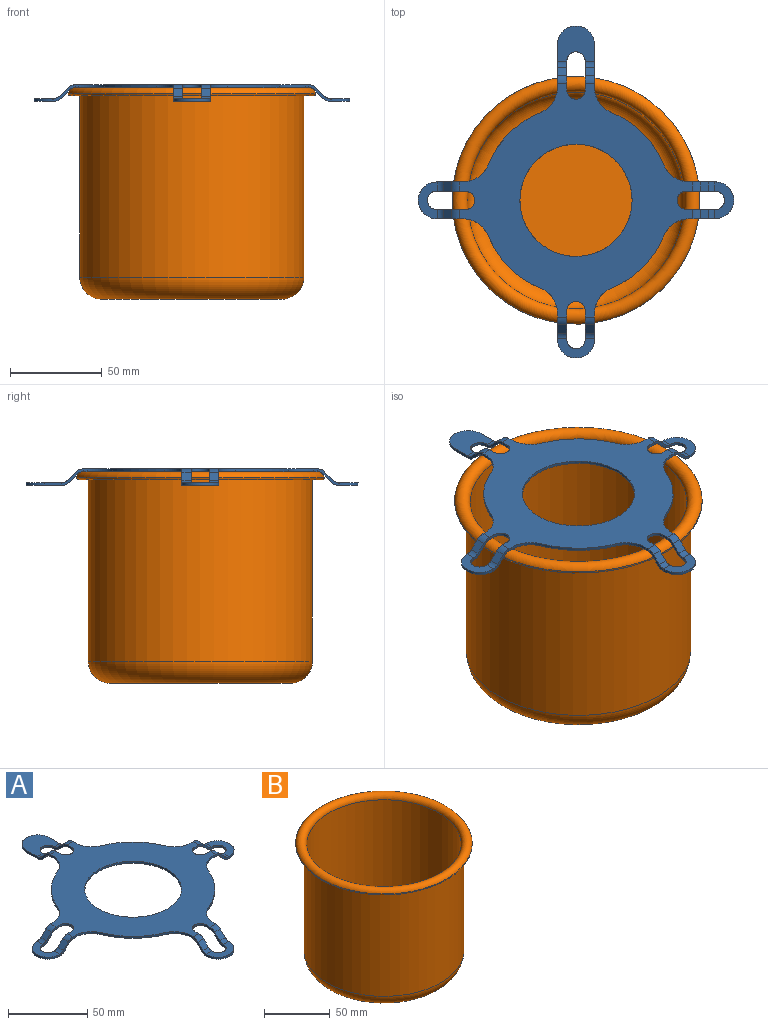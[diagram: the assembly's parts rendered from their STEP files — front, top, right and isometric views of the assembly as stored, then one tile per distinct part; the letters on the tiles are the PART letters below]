
ASSEMBLY  parts=2 mates=1
PART A: 163 faces, bbox 172.9x181.9x10 mm
  f0: plane 20x10.56mm, normal (0,0,-1), area 121.5mm2, adj f8,f9,f10,f11,f12,f13,f22,f23
  f1: plane 20x10.56mm, normal (0,0,-1), area 121.5mm2, adj f14,f15,f16,f17,f18,f19,f24,f25
  f2: plane 20x10.57mm, normal (0,0,-1), area 121.7mm2, adj f3,f4,f5,f6,f7,f20,f21,f26
  f3: cylinder r=10mm len=20mm, axis (0,0,1), area 47.1mm2, adj f2,f7,f20,f28
  f4: cylinder r=5mm len=10mm, axis (0,0,-1), area 23.6mm2, adj f2,f5,f6,f28
  f5: plane 1.5x0.39mm, normal (0,1,0), area 0.6mm2, adj f2,f4,f27,f28
  f6: plane 1.5x0.39mm, normal (0,-1,0), area 0.6mm2, adj f2,f4,f28,f29
  f7: plane 1.5x0.39mm, normal (0,1,0), area 0.6mm2, adj f2,f3,f28,f30
  f8: plane 1.5x0.38mm, normal (0,1,0), area 0.6mm2, adj f0,f9,f31,f33
  f9: cylinder r=10mm len=20mm, axis (0,0,1), area 47.1mm2, adj f0,f8,f13,f33
  f10: cylinder r=5mm len=10mm, axis (0,0,-1), area 23.6mm2, adj f0,f11,f12,f33
  f11: plane 1.5x0.39mm, normal (0,-1,0), area 0.6mm2, adj f0,f10,f32,f33
  f12: plane 1.5x0.39mm, normal (0,1,0), area 0.6mm2, adj f0,f10,f33,f34
  f13: plane 1.5x0.38mm, normal (0,-1,0), area 0.6mm2, adj f0,f9,f33,f35
  f14: plane 1.5x0.38mm, normal (-1,0,0), area 0.6mm2, adj f1,f15,f36,f38
  f15: cylinder r=10mm len=20mm, axis (0,0,1), area 47.1mm2, adj f1,f14,f19,f38
  f16: cylinder r=5mm len=10mm, axis (0,0,-1), area 23.6mm2, adj f1,f17,f18,f38
  f17: plane 1.5x0.39mm, normal (1,0,0), area 0.6mm2, adj f1,f16,f37,f38
  f18: plane 1.5x0.39mm, normal (-1,0,0), area 0.6mm2, adj f1,f16,f38,f39
  f19: plane 1.5x0.38mm, normal (1,0,0), area 0.6mm2, adj f1,f15,f38,f40
  f20: plane 1.5x0.39mm, normal (0,-1,0), area 0.6mm2, adj f2,f3,f28,f41
  f21: cylinder r=6mm len=5mm, axis (0,-1,0), area 23.6mm2, adj f2,f29,f30,f42
  f22: cylinder r=6mm len=5mm, axis (0,1,0), area 23.6mm2, adj f0,f31,f32,f43
  f23: cylinder r=6mm len=5mm, axis (0,1,0), area 23.6mm2, adj f0,f34,f35,f44
  f24: cylinder r=6mm len=5mm, axis (-1,0,0), area 23.6mm2, adj f1,f36,f37,f45
  f25: cylinder r=6mm len=5mm, axis (-1,0,0), area 23.6mm2, adj f1,f39,f40,f46
  f26: cylinder r=6mm len=5mm, axis (0,-1,0), area 23.6mm2, adj f2,f27,f41,f47
  f27: plane 4.24x2.82mm, normal (0,1,0), area 6.2mm2, adj f5,f26,f48,f49
  f28: plane 20.31x10.7mm, normal (0,0,1), area 122mm2, adj f3,f4,f5,f6,f7,f20,f48,f50
  f29: plane 4.24x2.82mm, normal (0,-1,0), area 6.2mm2, adj f6,f21,f50,f51
  f30: plane 4.24x2.82mm, normal (0,1,0), area 6.2mm2, adj f7,f21,f50,f52
  f31: plane 4.24x2.82mm, normal (0,1,0), area 6.2mm2, adj f8,f22,f53,f54
  f32: plane 4.24x2.82mm, normal (0,-1,0), area 6.2mm2, adj f11,f22,f53,f55
  f33: plane 20.31x10.69mm, normal (0,0,1), area 121.6mm2, adj f8,f9,f10,f11,f12,f13,f53,f56
  f34: plane 4.24x2.82mm, normal (0,1,0), area 6.2mm2, adj f12,f23,f56,f57
  f35: plane 4.24x2.82mm, normal (0,-1,0), area 6.2mm2, adj f13,f23,f56,f58
  f36: plane 4.24x2.82mm, normal (-1,0,0), area 6.2mm2, adj f14,f24,f59,f60
  f37: plane 4.24x2.82mm, normal (1,0,0), area 6.2mm2, adj f17,f24,f59,f61
  f38: plane 20.31x10.69mm, normal (0,0,1), area 121.5mm2, adj f14,f15,f16,f17,f18,f19,f59,f62
  f39: plane 4.24x2.82mm, normal (-1,0,0), area 6.2mm2, adj f18,f25,f62,f63
  f40: plane 4.24x2.82mm, normal (1,0,0), area 6.2mm2, adj f19,f25,f62,f64
  f41: plane 4.24x2.82mm, normal (0,-1,0), area 6.2mm2, adj f20,f26,f48,f65
  f42: plane 5x4.44mm, normal (-0.71,0,-0.71), area 31.4mm2, adj f21,f51,f52,f66
  f43: plane 5x4.44mm, normal (0.71,0,-0.71), area 31.4mm2, adj f22,f54,f55,f67
  f44: plane 5x4.44mm, normal (0.71,0,-0.71), area 31.4mm2, adj f23,f57,f58,f68
  f45: plane 5x4.44mm, normal (0,0.71,-0.71), area 31.4mm2, adj f24,f60,f61,f69
  f46: plane 5x4.44mm, normal (0,0.71,-0.71), area 31.4mm2, adj f25,f63,f64,f70
  f47: plane 5x4.44mm, normal (-0.71,0,-0.71), area 31.4mm2, adj f26,f49,f65,f71
  f48: cylinder r=4.5mm len=5mm, axis (0,-1,0), area 17.7mm2, adj f27,f28,f41,f72
  f49: plane 5.5x5.5mm, normal (0,1,0), area 9.4mm2, adj f27,f47,f72,f73
  f50: cylinder r=4.5mm len=5mm, axis (0,-1,0), area 17.7mm2, adj f28,f29,f30,f75
  f51: plane 5.5x5.5mm, normal (0,-1,0), area 9.4mm2, adj f29,f42,f74,f75
  f52: plane 5.5x5.5mm, normal (0,1,0), area 9.4mm2, adj f30,f42,f75,f76
  f53: cylinder r=4.5mm len=5mm, axis (0,1,0), area 17.7mm2, adj f31,f32,f33,f78
  f54: plane 5.5x5.5mm, normal (0,1,0), area 9.4mm2, adj f31,f43,f77,f78
  f55: plane 5.5x5.5mm, normal (0,-1,0), area 9.4mm2, adj f32,f43,f78,f79
  f56: cylinder r=4.5mm len=5mm, axis (0,1,0), area 17.7mm2, adj f33,f34,f35,f81
  f57: plane 5.5x5.5mm, normal (0,1,0), area 9.4mm2, adj f34,f44,f80,f81
  f58: plane 5.5x5.5mm, normal (0,-1,0), area 9.4mm2, adj f35,f44,f81,f82
  f59: cylinder r=4.5mm len=5mm, axis (-1,0,0), area 17.7mm2, adj f36,f37,f38,f84
  f60: plane 5.5x5.5mm, normal (-1,0,0), area 9.4mm2, adj f36,f45,f83,f84
  f61: plane 5.5x5.5mm, normal (1,0,0), area 9.4mm2, adj f37,f45,f84,f85
  f62: cylinder r=4.5mm len=5mm, axis (-1,0,0), area 17.7mm2, adj f38,f39,f40,f87
  f63: plane 5.5x5.5mm, normal (-1,0,0), area 9.4mm2, adj f39,f46,f86,f87
  f64: plane 5.5x5.5mm, normal (1,0,0), area 9.4mm2, adj f40,f46,f87,f88
  f65: plane 5.5x5.5mm, normal (0,-1,0), area 9.4mm2, adj f41,f47,f72,f89
  f66: cylinder r=4.5mm len=5mm, axis (0,-1,0), area 17.7mm2, adj f42,f74,f76,f90
  f67: cylinder r=4.5mm len=5mm, axis (0,1,0), area 17.7mm2, adj f43,f77,f79,f90
  f68: cylinder r=4.5mm len=5mm, axis (0,1,0), area 17.7mm2, adj f44,f80,f82,f90
  f69: cylinder r=4.5mm len=5mm, axis (-1,0,0), area 17.7mm2, adj f45,f83,f85,f90
  f70: cylinder r=4.5mm len=5mm, axis (-1,0,0), area 17.7mm2, adj f46,f86,f88,f90
  f71: cylinder r=4.5mm len=5mm, axis (0,-1,0), area 17.7mm2, adj f47,f73,f89,f90
  f72: plane 5x4.44mm, normal (0.71,0,0.71), area 31.4mm2, adj f48,f49,f65,f91
  f73: plane 4.24x2.82mm, normal (0,1,0), area 6.2mm2, adj f49,f71,f91,f92
  f74: plane 4.24x2.82mm, normal (0,-1,0), area 6.2mm2, adj f51,f66,f94,f95
  f75: plane 5x4.44mm, normal (0.71,0,0.71), area 31.4mm2, adj f50,f51,f52,f95
  f76: plane 4.24x2.82mm, normal (0,1,0), area 6.2mm2, adj f52,f66,f95,f96
  f77: plane 4.24x2.82mm, normal (0,1,0), area 6.2mm2, adj f54,f67,f105,f106
  f78: plane 5x4.44mm, normal (-0.71,0,0.71), area 31.4mm2, adj f53,f54,f55,f106
  f79: plane 4.24x2.82mm, normal (0,-1,0), area 6.2mm2, adj f55,f67,f106,f107
  f80: plane 4.24x2.82mm, normal (0,1,0), area 6.2mm2, adj f57,f68,f109,f110
  f81: plane 5x4.44mm, normal (-0.71,0,0.71), area 31.4mm2, adj f56,f57,f58,f110
  f82: plane 4.24x2.82mm, normal (0,-1,0), area 6.2mm2, adj f58,f68,f110,f111
  f83: plane 4.24x2.82mm, normal (-1,0,0), area 6.2mm2, adj f60,f69,f115,f116
  f84: plane 5x4.44mm, normal (0,-0.71,0.71), area 31.4mm2, adj f59,f60,f61,f116
  f85: plane 4.24x2.82mm, normal (1,0,0), area 6.2mm2, adj f61,f69,f116,f117
  f86: plane 4.24x2.82mm, normal (-1,0,0), area 6.2mm2, adj f63,f70,f119,f120
  f87: plane 5x4.44mm, normal (0,-0.71,0.71), area 31.4mm2, adj f62,f63,f64,f120
  f88: plane 4.24x2.82mm, normal (1,0,0), area 6.2mm2, adj f64,f70,f120,f121
  f89: plane 4.24x2.82mm, normal (0,-1,0), area 6.2mm2, adj f65,f71,f91,f125
  f90: plane 127.02x127.02mm, normal (0,0,-1), area 6269.3mm2, adj f66,f67,f68,f69,f70,f71,f92,f93
  f91: cylinder r=6mm len=5mm, axis (0,-1,0), area 23.6mm2, adj f72,f73,f89,f133
  f92: plane 3.52x1.5mm, normal (0,1,0), area 5.3mm2, adj f73,f90,f93,f133
  f93: cylinder r=5mm len=10mm, axis (0,0,-1), area 23.6mm2, adj f90,f92,f94,f133
  f94: plane 3.52x1.5mm, normal (0,-1,0), area 5.3mm2, adj f74,f90,f93,f133
  f95: cylinder r=6mm len=5mm, axis (0,-1,0), area 23.6mm2, adj f74,f75,f76,f133
  f96: plane 1.89x1.5mm, normal (0,1,0), area 2.8mm2, adj f76,f90,f97,f133
  f97: cylinder r=15mm len=13.9mm, axis (0,0,-1), area 26.7mm2, adj f90,f96,f98,f133
  f98: cylinder r=51.5mm len=28.36mm, axis (0,0,1), area 61.8mm2, adj f90,f97,f99,f133
  f99: cylinder r=15mm len=13.9mm, axis (0,0,-1), area 26.7mm2, adj f90,f98,f100,f133
  f100: plane 1.89x1.5mm, normal (1,0,0), area 2.8mm2, adj f90,f99,f132,f133
  f101: cylinder r=5mm len=10mm, axis (0,0,-1), area 23.6mm2, adj f90,f128,f129,f133
  f102: cylinder r=15mm len=13.9mm, axis (0,0,-1), area 26.7mm2, adj f90,f103,f127,f133
  f103: cylinder r=51.5mm len=28.36mm, axis (0,0,1), area 61.8mm2, adj f90,f102,f104,f133
  f104: cylinder r=15mm len=13.9mm, axis (0,0,-1), area 26.7mm2, adj f90,f103,f105,f133
  f105: plane 1.89x1.5mm, normal (0,1,0), area 2.8mm2, adj f77,f90,f104,f133
  f106: cylinder r=6mm len=5mm, axis (0,1,0), area 23.6mm2, adj f77,f78,f79,f133
  f107: plane 3.52x1.5mm, normal (0,-1,0), area 5.3mm2, adj f79,f90,f108,f133
  f108: cylinder r=5mm len=10mm, axis (0,0,-1), area 23.6mm2, adj f90,f107,f109,f133
  f109: plane 3.52x1.5mm, normal (0,1,0), area 5.3mm2, adj f80,f90,f108,f133
  f110: cylinder r=6mm len=5mm, axis (0,1,0), area 23.6mm2, adj f80,f81,f82,f133
  f111: plane 1.89x1.5mm, normal (0,-1,0), area 2.8mm2, adj f82,f90,f112,f133
  f112: cylinder r=15mm len=13.9mm, axis (0,0,-1), area 26.7mm2, adj f90,f111,f113,f133
  f113: cylinder r=51.5mm len=28.36mm, axis (0,0,1), area 61.8mm2, adj f90,f112,f114,f133
  f114: cylinder r=15mm len=13.9mm, axis (0,0,-1), area 26.7mm2, adj f90,f113,f115,f133
  f115: plane 1.89x1.5mm, normal (-1,0,0), area 2.8mm2, adj f83,f90,f114,f133
  f116: cylinder r=6mm len=5mm, axis (-1,0,0), area 23.6mm2, adj f83,f84,f85,f133
  f117: plane 3.52x1.5mm, normal (1,0,0), area 5.3mm2, adj f85,f90,f118,f133
  f118: cylinder r=5mm len=10mm, axis (0,0,-1), area 23.6mm2, adj f90,f117,f119,f133
  f119: plane 3.52x1.5mm, normal (-1,0,0), area 5.3mm2, adj f86,f90,f118,f133
  f120: cylinder r=6mm len=5mm, axis (-1,0,0), area 23.6mm2, adj f86,f87,f88,f133
  f121: plane 1.89x1.5mm, normal (1,0,0), area 2.8mm2, adj f88,f90,f122,f133
  f122: cylinder r=15mm len=13.9mm, axis (0,0,-1), area 26.7mm2, adj f90,f121,f123,f133
  f123: cylinder r=51.5mm len=28.36mm, axis (0,0,1), area 61.8mm2, adj f90,f122,f124,f133
  f124: cylinder r=15mm len=13.9mm, axis (0,0,-1), area 26.7mm2, adj f90,f123,f125,f133
  f125: plane 1.89x1.5mm, normal (0,-1,0), area 2.8mm2, adj f89,f90,f124,f133
  f126: cylinder r=30.5mm len=61mm, axis (0,0,-1), area 287.5mm2, adj f90,f133
  f127: plane 1.89x1.5mm, normal (-1,0,0), area 2.8mm2, adj f90,f102,f133,f134
  f128: plane 3.52x1.5mm, normal (1,0,0), area 5.3mm2, adj f90,f101,f133,f135
  f129: plane 3.52x1.5mm, normal (-1,0,0), area 5.3mm2, adj f90,f101,f133,f136
  f130: cylinder r=4.5mm len=5mm, axis (1,0,0), area 17.7mm2, adj f90,f134,f135,f137
  f131: cylinder r=4.5mm len=5mm, axis (1,0,0), area 17.7mm2, adj f90,f132,f136,f138
  f132: plane 4.24x2.82mm, normal (1,0,0), area 6.2mm2, adj f100,f131,f139,f140
  f133: plane 127.99x127.99mm, normal (0,0,1), area 6276mm2, adj f91,f92,f93,f94,f95,f96,f97,f98
  f134: plane 4.24x2.82mm, normal (-1,0,0), area 6.2mm2, adj f127,f130,f141,f142
  f135: plane 4.24x2.82mm, normal (1,0,0), area 6.2mm2, adj f128,f130,f142,f143
  f136: plane 4.24x2.82mm, normal (-1,0,0), area 6.2mm2, adj f129,f131,f139,f144
  f137: plane 5x4.44mm, normal (0,-0.71,-0.71), area 31.4mm2, adj f130,f141,f143,f145
  f138: plane 5x4.44mm, normal (0,-0.71,-0.71), area 31.4mm2, adj f131,f140,f144,f146
  f139: cylinder r=6mm len=5mm, axis (1,0,0), area 23.6mm2, adj f132,f133,f136,f147
  f140: plane 5.5x5.5mm, normal (1,0,0), area 9.4mm2, adj f132,f138,f147,f148
  f141: plane 5.5x5.5mm, normal (-1,0,0), area 9.4mm2, adj f134,f137,f149,f150
  f142: cylinder r=6mm len=5mm, axis (1,0,0), area 23.6mm2, adj f133,f134,f135,f150
  f143: plane 5.5x5.5mm, normal (1,0,0), area 9.4mm2, adj f135,f137,f150,f151
  f144: plane 5.5x5.5mm, normal (-1,0,0), area 9.4mm2, adj f136,f138,f147,f152
  f145: cylinder r=6mm len=5mm, axis (1,0,0), area 23.6mm2, adj f137,f149,f151,f153
  f146: cylinder r=6mm len=5mm, axis (1,0,0), area 23.6mm2, adj f138,f148,f152,f153
  f147: plane 5x4.44mm, normal (0,0.71,0.71), area 31.4mm2, adj f139,f140,f144,f154
  f148: plane 4.24x2.82mm, normal (1,0,0), area 6.2mm2, adj f140,f146,f154,f155
  f149: plane 4.24x2.82mm, normal (-1,0,0), area 6.2mm2, adj f141,f145,f157,f158
  f150: plane 5x4.44mm, normal (0,0.71,0.71), area 31.4mm2, adj f141,f142,f143,f158
  f151: plane 4.24x2.82mm, normal (1,0,0), area 6.2mm2, adj f143,f145,f158,f159
  f152: plane 4.24x2.82mm, normal (-1,0,0), area 6.2mm2, adj f144,f146,f154,f161
  f153: plane 20x19.63mm, normal (0,0,-1), area 302.8mm2, adj f145,f146,f155,f156,f157,f159,f160,f161
  f154: cylinder r=4.5mm len=5mm, axis (1,0,0), area 17.7mm2, adj f147,f148,f152,f162
  f155: plane 9.44x1.5mm, normal (1,0,0), area 14.2mm2, adj f148,f153,f156,f162
  f156: cylinder r=10mm len=20mm, axis (0,0,1), area 47.1mm2, adj f153,f155,f157,f162
  f157: plane 9.44x1.5mm, normal (-1,0,0), area 14.2mm2, adj f149,f153,f156,f162
  f158: cylinder r=4.5mm len=5mm, axis (1,0,0), area 17.7mm2, adj f149,f150,f151,f162
  f159: plane 1.5x0.39mm, normal (1,0,0), area 0.6mm2, adj f151,f153,f160,f162
  f160: cylinder r=5mm len=10mm, axis (0,0,-1), area 23.6mm2, adj f153,f159,f161,f162
  f161: plane 1.5x0.39mm, normal (-1,0,0), area 0.6mm2, adj f152,f153,f160,f162
  f162: plane 20.31x19.76mm, normal (0,0,1), area 302.8mm2, adj f154,f155,f156,f157,f158,f159,f160,f161
PART B: 9 faces, bbox 146.1x146.1x115 mm
  f0: cylinder r=61mm len=122mm, axis (0,0,-1), area 37848.3mm2, adj f1,f8
  f1: torus R=63.25mm, axis (0,0,-1), area 2519.7mm2, adj f0,f2
  f2: torus R=66.34mm, axis (0,0,-1), area 1313.4mm2, adj f1,f3
  f3: torus R=63.25mm, axis (0,0,-1), area 4743mm2, adj f2,f4
  f4: cylinder r=59mm len=118mm, axis (0,0,-1), area 36607.4mm2, adj f3,f5
  f5: torus R=49mm, axis (0,0,-1), area 5464.4mm2, adj f4,f6
  f6: plane 98x98mm, normal (0,0,1), area 7543mm2, adj f5
  f7: plane 98x98mm, normal (0,0,-1), area 7543mm2, adj f8
  f8: torus R=49mm, axis (0,0,-1), area 6708.1mm2, adj f0,f7
PLACE A t=(-208.29,-37.81,183.07)mm
PLACE B t=(-119.68,50.8,67.97)mm
MATE cylindrical B.f0 <-> A.f98  axis (0,0,-1) through (-119.68,50.8,129.34)mm
